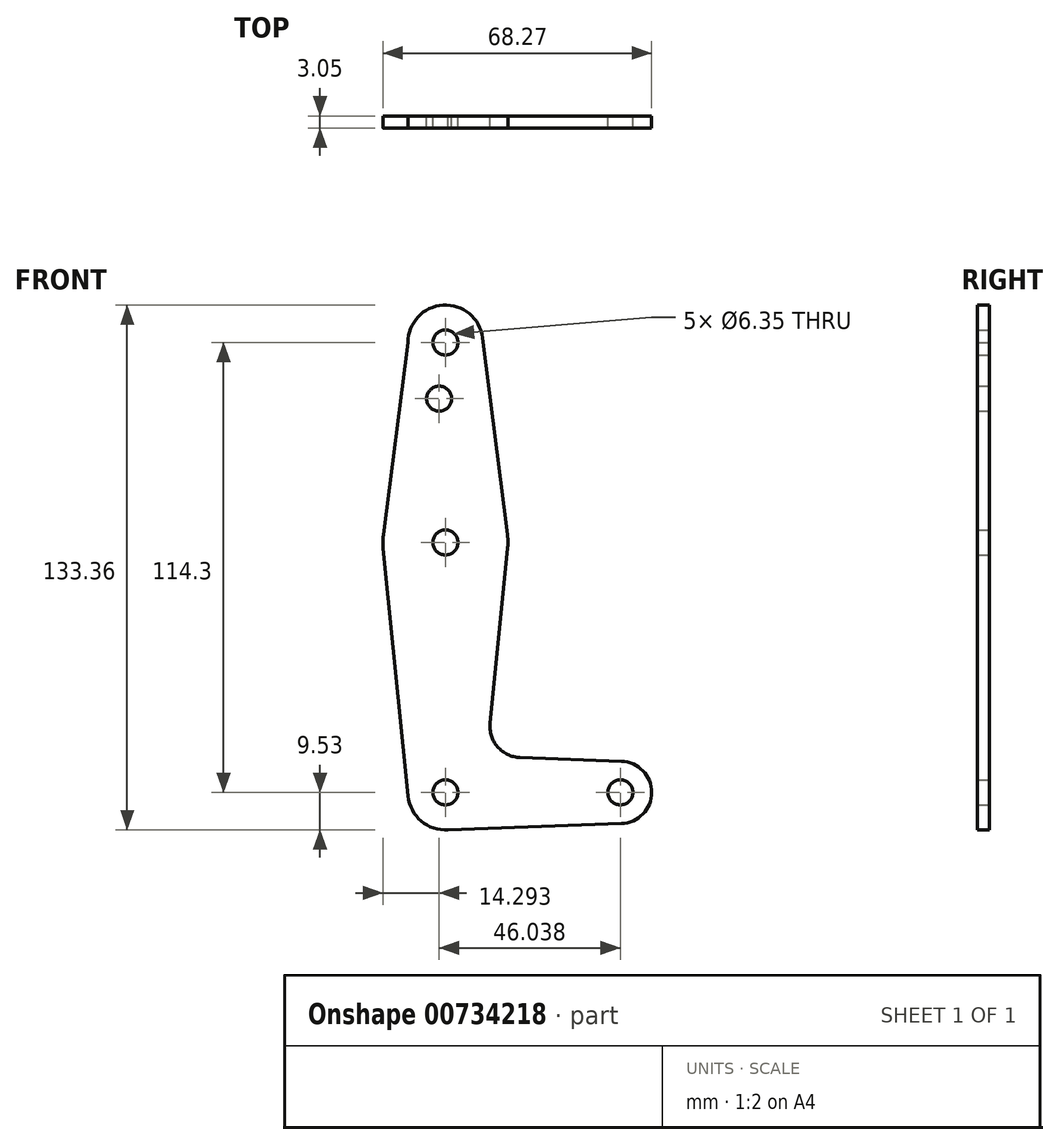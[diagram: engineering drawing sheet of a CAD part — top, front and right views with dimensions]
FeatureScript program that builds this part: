
annotation { "Feature Type Name" : "Feature", "Feature Type Description" : "" }
export const myFeature = defineFeature(function(context is Context, id is Id, definition is map)
    precondition{}
    {
        {
            var Q0;
            Q0=qCreatedBy(makeId("Front.planeOp"),FACE);
            var sketch = newSketch(context, id + "F0", { "sketchPlane" : qUnion([Q0])});
            skLineSegment(sketch, "E0", {"start": v(0, 114.3) * mm, "end": v(0, 0) * mm, "construction": true});
            skLineSegment(sketch, "E1", {"start": v(0, 0) * mm, "end": v(44.45, 0) * mm, "construction": true});
            skCircle(sketch, "E2", {"center": v(0, 114.3) * mm, "radius": 9.53 * mm});
            skCircle(sketch, "E3", {"center": v(0, 63.5) * mm, "radius": 15.88 * mm});
            skCircle(sketch, "E4", {"center": v(0, 0) * mm, "radius": 9.53 * mm});
            skCircle(sketch, "E5", {"center": v(44.45, 0) * mm, "radius": 7.94 * mm});
            skLineSegment(sketch, "E6", {"start": v(15.75, 65.48) * mm, "end": v(9.45, 115.5) * mm});
            skLineSegment(sketch, "E7", {"start": v(-9.53, 114.3) * mm, "end": v(-15.75, 65.5) * mm});
            skLineSegment(sketch, "E8", {"start": v(0, -9.53) * mm, "end": v(44.73, -7.93) * mm});
            skCircle(sketch, "E9", {"center": v(0, 114.3) * mm, "radius": 3.18 * mm});
            skCircle(sketch, "E10", {"center": v(0, 0) * mm, "radius": 3.18 * mm});
            skCircle(sketch, "E11", {"center": v(44.45, 0) * mm, "radius": 3.18 * mm});
            skCircle(sketch, "E12", {"center": v(-1.59, 100.03) * mm, "radius": 3.18 * mm});
            skCircle(sketch, "E13", {"center": v(0, 63.5) * mm, "radius": 3.18 * mm});
            skLineSegment(sketch, "E14", {"start": v(-15.8, 61.91) * mm, "end": v(-9.48, -0.95) * mm});
            skLineSegment(sketch, "E15", {"start": v(15.8, 61.91) * mm, "end": v(11.34, 17.6) * mm});
            skLineSegment(sketch, "E16", {"start": v(18.97, 8.85) * mm, "end": v(44.73, 7.93) * mm});
            skArc(sketch, "E17.filletArc", {"start": v(11.34, 17.6) * mm, "mid": v(13.26, 11.57) * mm, "end": v(18.97, 8.85) * mm});
            skSolve(sketch);
        }
        {
            var Q0;
            Q0 = qSketchRegion(id + "F0", true);
            extrude(context, id + "F1", {"entities" : qUnion([Q0]), "depth" : 3.05 * mm, "offsetDistance" : 25.4 * mm});
        }
    });
